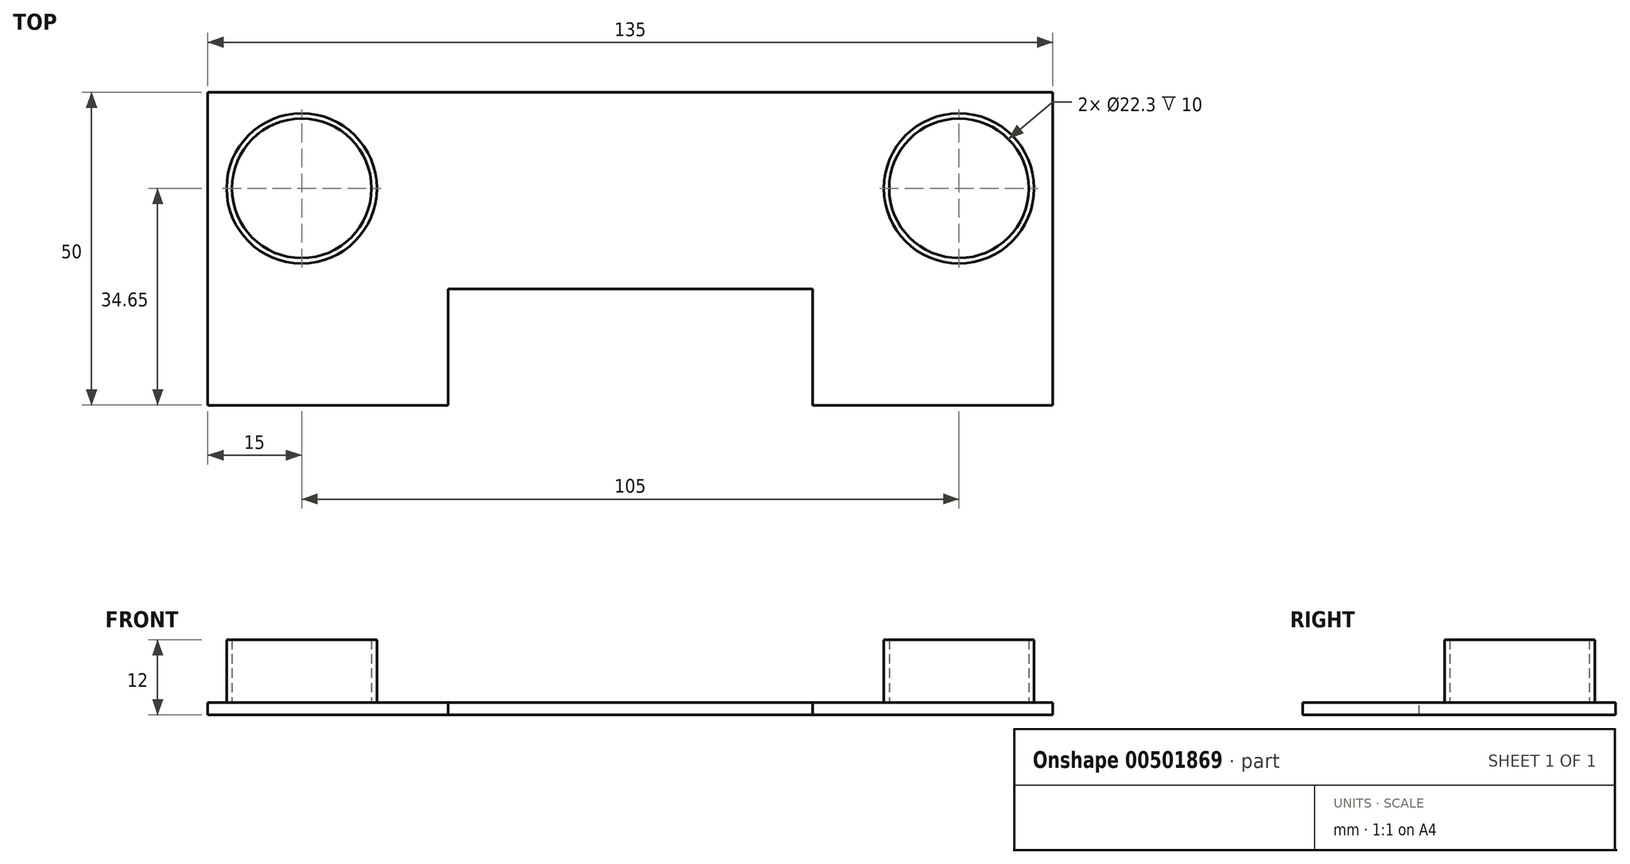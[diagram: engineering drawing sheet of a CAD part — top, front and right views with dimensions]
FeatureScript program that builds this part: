
annotation { "Feature Type Name" : "Feature", "Feature Type Description" : "" }
export const myFeature = defineFeature(function(context is Context, id is Id, definition is map)
    precondition{}
    {
        {
            var Q0;
            Q0=qCreatedBy(makeId("Top.planeOp"),FACE);
            var sketch = newSketch(context, id + "F0", { "sketchPlane" : qUnion([Q0])});
            skPoint(sketch, "E0.middle", {"position": v(0, 0) * mm});
            skCircle(sketch, "E1", {"center": v(-52.5, 0) * mm, "radius": 11.15 * mm});
            skCircle(sketch, "E2", {"center": v(52.5, 0) * mm, "radius": 11.15 * mm});
            skCircle(sketch, "E3", {"center": v(-52.5, 0) * mm, "radius": 12 * mm});
            skCircle(sketch, "E4", {"center": v(52.5, 0) * mm, "radius": 12 * mm});
            skSolve(sketch);
        }
        {
            var Q0;
            Q0 = qSketchRegion(id + "F0", true);
            extrude(context, id + "F1", {"entities" : qUnion([Q0]), "depth" : 10 * mm});
        }
        {
            var Q0;
            Q0=qCreatedBy(makeId("Top.planeOp"),FACE);
            var sketch = newSketch(context, id + "F2", { "sketchPlane" : qUnion([Q0])});
            skLineSegment(sketch, "E5.bottom", {"start": v(67.5, -34.65) * mm, "end": v(-67.5, -34.65) * mm});
            skLineSegment(sketch, "E5.top", {"start": v(67.5, 15.35) * mm, "end": v(-67.5, 15.35) * mm});
            skLineSegment(sketch, "E5.left", {"start": v(67.5, -34.65) * mm, "end": v(67.5, 15.35) * mm});
            skLineSegment(sketch, "E5.right", {"start": v(-67.5, -34.65) * mm, "end": v(-67.5, 15.35) * mm});
            skPoint(sketch, "E5.middle", {"position": v(0, -9.65) * mm});
            skSolve(sketch);
        }
        {
            var Q0;
            Q0 = qSketchRegion(id + "F2", true);
            extrude(context, id + "F3", {"entities" : qUnion([Q0]), "oppositeDirection" : true, "depth" : 2 * mm});
        }
        {
            var Q0;
            Q0=makeQuery(id+"F3.opExtrude","CAP_FACE",FACE,{"disambiguationData":[OSD([sQuery(id+"F2.wireOp",EDGE,"E5.bottom"),sQuery(id+"F2.wireOp",EDGE,"E5.top"),sQuery(id+"F2.wireOp",EDGE,"E5.left"),sQuery(id+"F2.wireOp",EDGE,"E5.right")])],"isStart":true});
            var sketch = newSketch(context, id + "F4", { "sketchPlane" : qUnion([Q0])});
            skLineSegment(sketch, "E6.bottom", {"start": v(29.12, -53.24) * mm, "end": v(-29.12, -53.24) * mm});
            skLineSegment(sketch, "E6.top", {"start": v(29.12, -16.06) * mm, "end": v(-29.12, -16.06) * mm});
            skLineSegment(sketch, "E6.left", {"start": v(29.12, -53.24) * mm, "end": v(29.12, -16.06) * mm});
            skLineSegment(sketch, "E6.right", {"start": v(-29.12, -53.24) * mm, "end": v(-29.12, -16.06) * mm});
            skPoint(sketch, "E6.middle", {"position": v(0, -34.65) * mm});
            skSolve(sketch);
        }
        {
            var Q0;
            Q0 = qSketchRegion(id + "F4", true);
            extrude(context, id + "F5", {"entities" : qUnion([Q0]), "operationType" : NewBodyOperationType.REMOVE, "oppositeDirection" : true, "depth" : 25.4 * mm});
        }
    });
